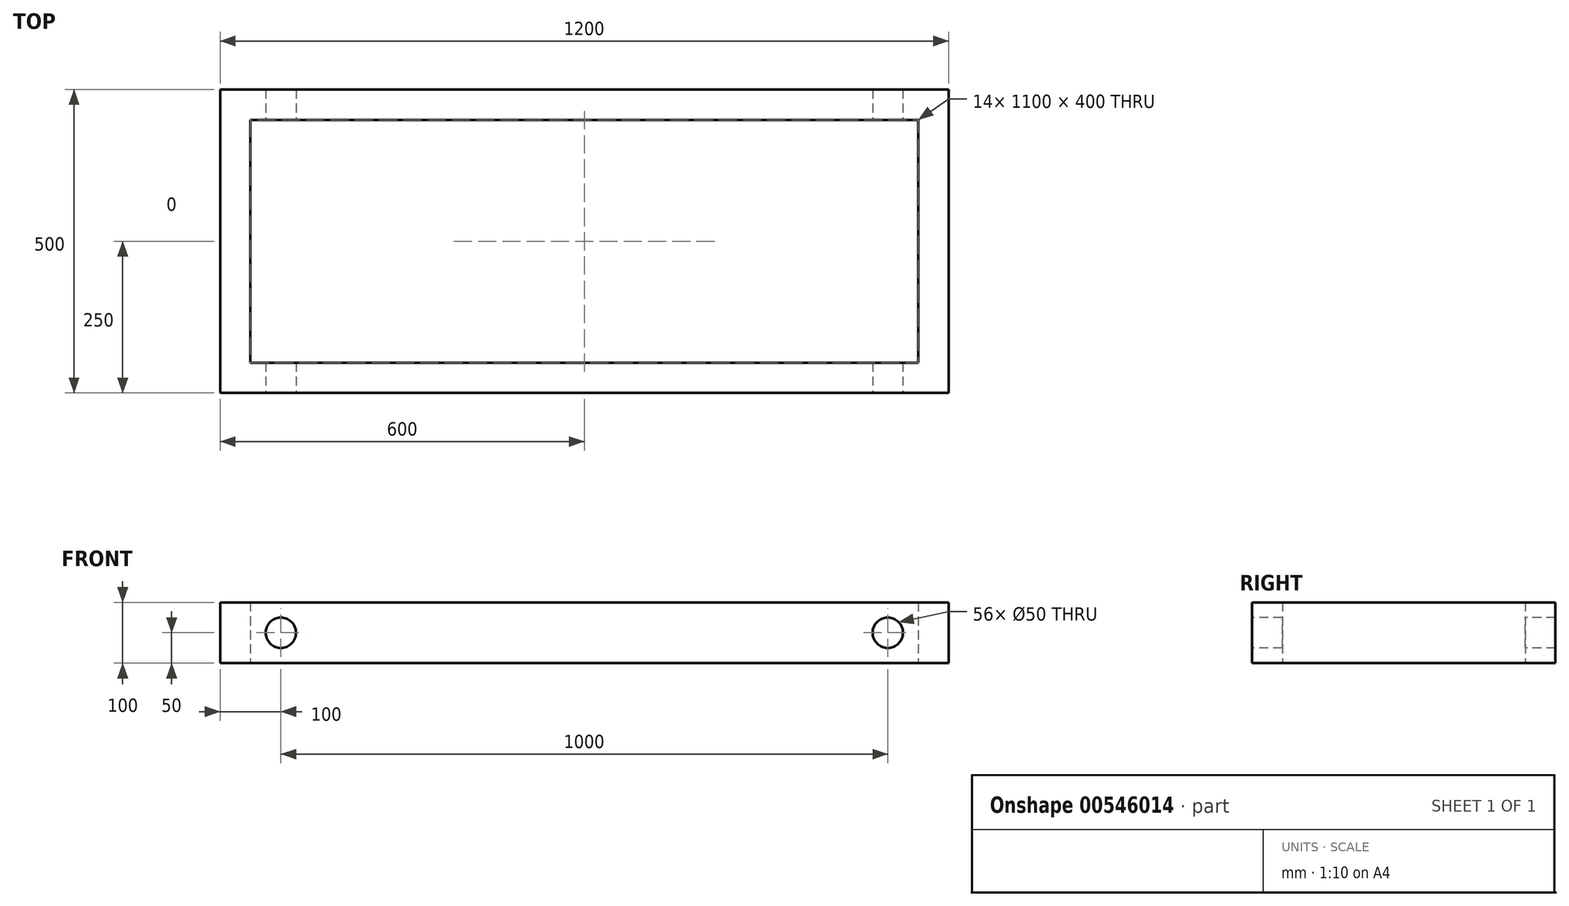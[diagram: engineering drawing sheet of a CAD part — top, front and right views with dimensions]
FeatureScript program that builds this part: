
annotation { "Feature Type Name" : "Feature", "Feature Type Description" : "" }
export const myFeature = defineFeature(function(context is Context, id is Id, definition is map)
    precondition{}
    {
        {
            var Q0;
            Q0=qCreatedBy(makeId("Top.planeOp"),FACE);
            var sketch = newSketch(context, id + "F0", { "sketchPlane" : qUnion([Q0])});
            skLineSegment(sketch, "E0.bottom", {"start": v(550, 200) * mm, "end": v(-550, 200) * mm});
            skLineSegment(sketch, "E0.top", {"start": v(550, -200) * mm, "end": v(-550, -200) * mm});
            skLineSegment(sketch, "E0.left", {"start": v(550, 200) * mm, "end": v(550, -200) * mm});
            skLineSegment(sketch, "E0.right", {"start": v(-550, 200) * mm, "end": v(-550, -200) * mm});
            skPoint(sketch, "E0.middle", {"position": v(0, 0) * mm});
            skLineSegment(sketch, "E1.bottom", {"start": v(600, 250) * mm, "end": v(-600, 250) * mm});
            skLineSegment(sketch, "E1.top", {"start": v(600, -250) * mm, "end": v(-600, -250) * mm});
            skLineSegment(sketch, "E1.left", {"start": v(600, 250) * mm, "end": v(600, -250) * mm});
            skLineSegment(sketch, "E1.right", {"start": v(-600, 250) * mm, "end": v(-600, -250) * mm});
            skLineSegment(sketch, "E2", {"start": v(-550, 0) * mm, "end": v(-600, 0) * mm, "construction": true});
            skLineSegment(sketch, "E3", {"start": v(0, -200) * mm, "end": v(0, -250) * mm, "construction": true});
            skSolve(sketch);
        }
        {
            var Q0;
            Q0 = qSketchRegion(id + "F0", true);
            extrude(context, id + "F1", {"entities" : qUnion([Q0]), "endBound" : BoundingType.SYMMETRIC, "depth" : 100 * mm, "offsetDistance" : 25 * mm});
        }
        {
            var Q0;
            Q0=qCreatedBy(makeId("Front.planeOp"),FACE);
            var sketch = newSketch(context, id + "F2", { "sketchPlane" : qUnion([Q0])});
            skLineSegment(sketch, "E4", {"start": v(0, 0) * mm, "end": v(-500, 0) * mm});
            skLineSegment(sketch, "E5", {"start": v(0, 0) * mm, "end": v(500, 0) * mm});
            skCircle(sketch, "E6", {"center": v(-500, 0) * mm, "radius": 25 * mm});
            skCircle(sketch, "E7", {"center": v(500, 0) * mm, "radius": 25 * mm});
            skSolve(sketch);
        }
        {
            var Q0;
            Q0 = qSketchRegion(id + "F2", true);
            extrude(context, id + "F3", {"entities" : qUnion([Q0]), "operationType" : NewBodyOperationType.REMOVE, "endBound" : BoundingType.THROUGH_ALL, "oppositeDirection" : true, "depth" : 25 * mm, "offsetDistance" : 25 * mm, "hasSecondDirection" : true, "secondDirectionBound" : SecondDirectionBoundingType.THROUGH_ALL, "secondDirectionOppositeDirection" : false, "secondDirectionDepth" : 25 * mm});
        }
    });
